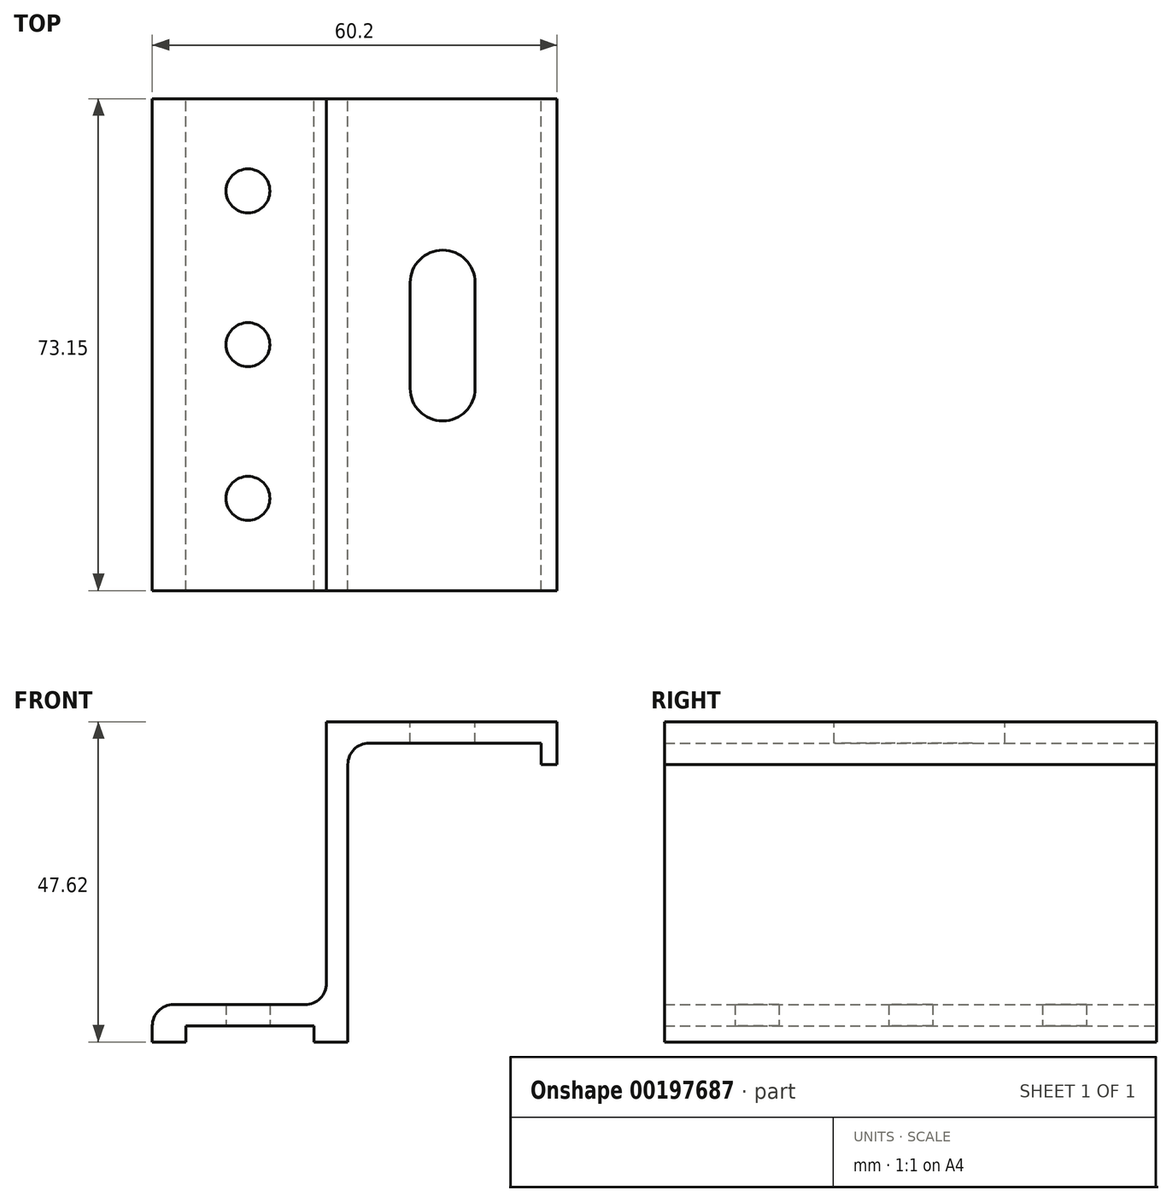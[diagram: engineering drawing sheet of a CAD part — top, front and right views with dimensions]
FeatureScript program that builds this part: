
annotation { "Feature Type Name" : "Feature", "Feature Type Description" : "" }
export const myFeature = defineFeature(function(context is Context, id is Id, definition is map)
    precondition{}
    {
        {
            var Q0;
            Q0=qCreatedBy(makeId("Front.planeOp"),FACE);
            var sketch = newSketch(context, id + "F0", { "sketchPlane" : qUnion([Q0])});
            skLineSegment(sketch, "E0", {"start": v(32.52, 15.16) * mm, "end": v(-1.77, 15.16) * mm});
            skLineSegment(sketch, "E1", {"start": v(-1.77, 15.16) * mm, "end": v(-1.77, -26.9) * mm});
            skLineSegment(sketch, "E2", {"start": v(-1.77, -26.9) * mm, "end": v(-27.68, -26.9) * mm});
            skLineSegment(sketch, "E3", {"start": v(-27.68, -26.9) * mm, "end": v(-27.68, -32.46) * mm});
            skLineSegment(sketch, "E4", {"start": v(-27.68, -32.46) * mm, "end": v(-22.66, -32.46) * mm});
            skLineSegment(sketch, "E5", {"start": v(1.4, -32.46) * mm, "end": v(1.4, 11.99) * mm});
            skLineSegment(sketch, "E6", {"start": v(1.4, 11.99) * mm, "end": v(30.14, 11.99) * mm});
            skLineSegment(sketch, "E7", {"start": v(32.52, 11.99) * mm, "end": v(32.52, 15.16) * mm});
            skLineSegment(sketch, "E8.top", {"start": v(32.52, 8.81) * mm, "end": v(30.14, 8.81) * mm});
            skLineSegment(sketch, "E8.left", {"start": v(32.52, 11.99) * mm, "end": v(32.52, 8.81) * mm});
            skLineSegment(sketch, "E8.right", {"start": v(30.14, 11.99) * mm, "end": v(30.14, 8.81) * mm});
            skPoint(sketch, "E9.firstSnap0", {"position": v(30.14, 10.4) * mm});
            skLineSegment(sketch, "E10.top", {"start": v(-3.6, -30.08) * mm, "end": v(-22.66, -30.08) * mm});
            skLineSegment(sketch, "E10.left", {"start": v(-3.6, -32.46) * mm, "end": v(-3.6, -30.08) * mm});
            skLineSegment(sketch, "E10.right", {"start": v(-22.66, -32.46) * mm, "end": v(-22.66, -30.08) * mm});
            skLineSegment(sketch, "E11.trimOffspring", {"start": v(-3.6, -32.46) * mm, "end": v(1.4, -32.46) * mm});
            skLineSegment(sketch, "E12", {"start": v(-3.6, -30.08) * mm, "end": v(1.4, -30.08) * mm, "construction": true});
            skLineSegment(sketch, "E13", {"start": v(-22.66, -30.08) * mm, "end": v(-27.68, -30.08) * mm, "construction": true});
            skSolve(sketch);
        }
        {
            var Q0;
            Q0 = qSketchRegion(id + "F0", true);
            extrude(context, id + "F1", {"entities" : qUnion([Q0]), "depth" : 73.15 * mm});
        }
        {
            var Q0;
            Q0=makeQuery(id+"F1.opExtrude","SWEPT_FACE",FACE,{"disambiguationData":[OSD([sQuery(id+"F0.wireOp",EDGE,"E10.top")])]});
            var sketch = newSketch(context, id + "F2", { "sketchPlane" : qUnion([Q0])});
            skPoint(sketch, "E14", {"position": v(-13.45, 13.72) * mm});
            skPoint(sketch, "E15", {"position": v(-13.45, 59.44) * mm});
            skPoint(sketch, "E16", {"position": v(-13.45, 36.58) * mm});
            skLineSegment(sketch, "E17", {"start": v(-13.45, 59.44) * mm, "end": v(-13.45, 36.58) * mm, "construction": true});
            skLineSegment(sketch, "E18", {"start": v(-13.45, 13.72) * mm, "end": v(-13.45, 36.58) * mm, "construction": true});
            skSolve(sketch);
        }
        {
            var Q0;
            Q0=sQuery(id+"F2.wireOp",VERTEX,"E14");
            var Q1;
            Q1=sQuery(id+"F2.wireOp",VERTEX,"E16");
            var Q2;
            Q2=sQuery(id+"F2.wireOp",VERTEX,"E15");
            var Q3;
            Q3=makeQuery(id+"F1.opExtrude","SWEPT_BODY",BODY,{"disambiguationData":[OSD([sQuery(id+"F0.wireOp",EDGE,"E0"),sQuery(id+"F0.wireOp",EDGE,"E1"),sQuery(id+"F0.wireOp",EDGE,"E2"),sQuery(id+"F0.wireOp",EDGE,"E3"),sQuery(id+"F0.wireOp",EDGE,"E4"),sQuery(id+"F0.wireOp",EDGE,"E5"),sQuery(id+"F0.wireOp",EDGE,"E6"),sQuery(id+"F0.wireOp",EDGE,"E7"),sQuery(id+"F0.wireOp",EDGE,"E8.top"),sQuery(id+"F0.wireOp",EDGE,"E8.left"),sQuery(id+"F0.wireOp",EDGE,"E8.right"),sQuery(id+"F0.wireOp",EDGE,"E10.top"),sQuery(id+"F0.wireOp",EDGE,"E10.left"),sQuery(id+"F0.wireOp",EDGE,"E10.right"),sQuery(id+"F0.wireOp",EDGE,"E11.trimOffspring")])]});
            hole(context, id + "F3", {"style" : HoleStyle.SIMPLE, "endStyle" : HoleEndStyle.THROUGH, "standardTappedOrClearance" : lookupTablePath({ "standard" : "ANSI", "fit" : "Close", "size" : "1/4", "type" : "Clearance" }), "standardBlindInLast" : lookupTablePath({ "fit" : "Close", "standard" : "ANSI", "size" : "1/4", "type" : "Clearance" }), "holeDiameter" : 6.53 * mm, "locations" : qUnion([Q0, Q1, Q2]), "scope" : qUnion([Q3]), "isTappedThrough" : true});
        }
        {
            var Q0;
            Q0=makeQuery(id+"F1.opExtrude","SWEPT_FACE",FACE,{"disambiguationData":[OSD([sQuery(id+"F0.wireOp",EDGE,"E0")])]});
            var sketch = newSketch(context, id + "F4", { "sketchPlane" : qUnion([Q0])});
            skLineSegment(sketch, "E19.left", {"start": v(10.68, -27.36) * mm, "end": v(10.68, -43.1) * mm});
            skLineSegment(sketch, "E19.right", {"start": v(20.33, -27.36) * mm, "end": v(20.33, -43.1) * mm});
            skPoint(sketch, "E20", {"position": v(20.33, -35.23) * mm});
            skArc(sketch, "E21", {"start": v(20.33, -27.36) * mm, "mid": v(15.5, -22.53) * mm, "end": v(10.68, -27.36) * mm});
            skArc(sketch, "E22", {"start": v(20.33, -43.1) * mm, "mid": v(15.5, -47.93) * mm, "end": v(10.68, -43.1) * mm});
            skPoint(sketch, "E23", {"position": v(15.5, -22.53) * mm});
            skPoint(sketch, "E24", {"position": v(15.5, -47.93) * mm});
            skSolve(sketch);
        }
        {
            var Q0;
            Q0=makeQuery(id+"F4.imprint","IMPRINT",FACE,{"disambiguationData":[TD([[makeQuery(id+"F4.imprint","IMPRINT",EDGE,{"derivedFrom":sQuery(id+"F4.wireOp",EDGE,"E19.left")}),1.0]])]});
            var Q1;
            Q1=sQuery(id+"F4.wireOp",EDGE,"B79mEKsK-oXH8-pD76-w7S3-O4mO0craSzWd");
            var Q2;
            Q2=sQuery(id+"F4.wireOp",EDGE,"8ef730a4-cce9-4130-b617-8e8b5dc9e550.0.1.6");
            var Q3;
            Q3=sQuery(id+"F4.wireOp",EDGE,"OuHG3wXi-NwYD-qbxj-Jqmp-a6nQJQTEx7GX");
            var Q4;
            Q4=sQuery(id+"F4.wireOp",EDGE,"8ef730a4-cce9-4130-b617-8e8b5dc9e550.0.1.4");
            var Q5;
            Q5=sQuery(id+"F4.wireOp",EDGE,"Ap6D9dI3-RrlL-FjQJ-PwrX-lJZBjQ6R1ei9");
            var Q6;
            Q6=sQuery(id+"F4.wireOp",EDGE,"Hr3Cz562-CN3z-GlAR-VMzT-rjX5pLILEnlI");
            var Q7;
            Q7=sQuery(id+"F4.wireOp",EDGE,"8ef730a4-cce9-4130-b617-8e8b5dc9e550.0.1.5");
            var Q8;
            Q8=sQuery(id+"F4.wireOp",EDGE,"8ef730a4-cce9-4130-b617-8e8b5dc9e550.0.1.3");
            extrude(context, id + "F5", {"entities" : qUnion([Q0]), "operationType" : NewBodyOperationType.REMOVE, "surfaceEntities" : qUnion([Q1, Q2, Q3, Q4, Q5, Q6, Q7, Q8]), "endBound" : BoundingType.THROUGH_ALL, "oppositeDirection" : true, "depth" : 25.4 * mm});
        }
        {
            var Q0;
            Q0=makeQuery(id+"F1.opExtrude","SWEPT_EDGE",EDGE,{"disambiguationData":[OSD([sQuery(id+"F0.wireOp",EDGE,"E1"),sQuery(id+"F0.wireOp",EDGE,"E2")])]});
            var Q1;
            Q1=makeQuery(id+"F1.opExtrude","SWEPT_EDGE",EDGE,{"disambiguationData":[OSD([sQuery(id+"F0.wireOp",EDGE,"E5"),sQuery(id+"F0.wireOp",EDGE,"E6")])]});
            var Q2;
            Q2=makeQuery(id+"F1.opExtrude","SWEPT_EDGE",EDGE,{"disambiguationData":[OSD([sQuery(id+"F0.wireOp",EDGE,"E2"),sQuery(id+"F0.wireOp",EDGE,"E3")])]});
            fillet(context, id + "F6", {"entities" : qUnion([Q0, Q1, Q2]), "radius" : 3.17 * mm, "allowEdgeOverflow" : false});
        }
    });
